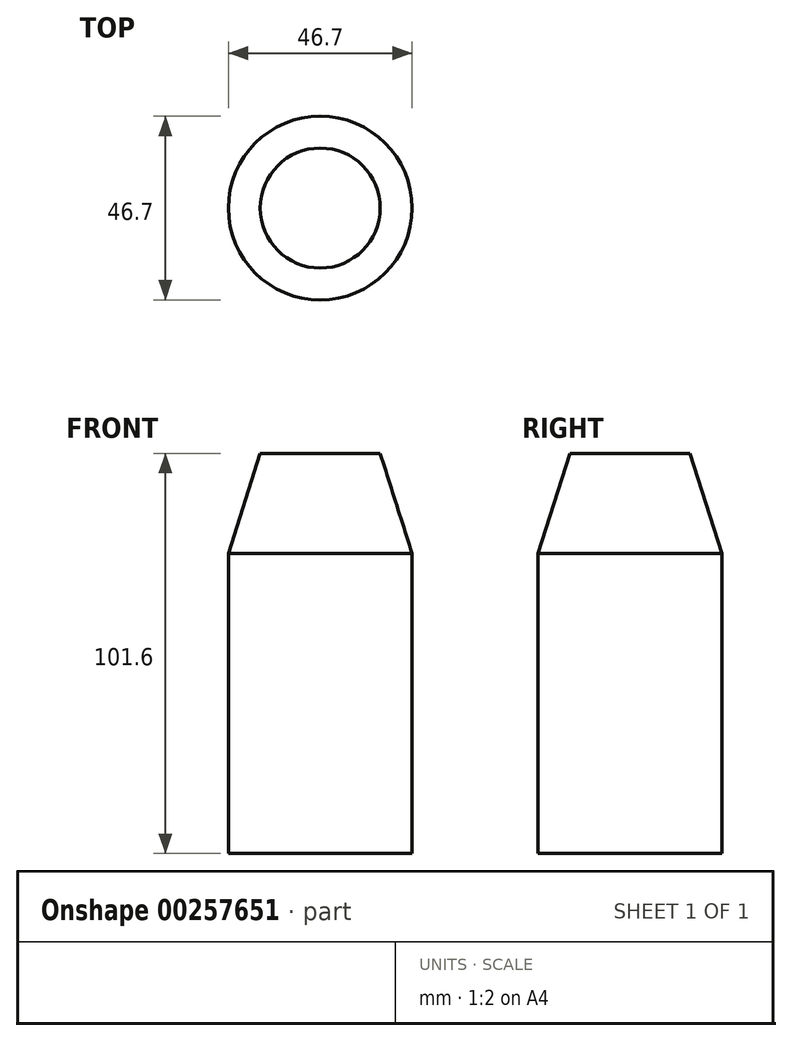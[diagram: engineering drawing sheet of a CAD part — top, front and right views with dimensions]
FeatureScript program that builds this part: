
annotation { "Feature Type Name" : "Feature", "Feature Type Description" : "" }
export const myFeature = defineFeature(function(context is Context, id is Id, definition is map)
    precondition{}
    {
        {
            var Q0;
            Q0=qCreatedBy(makeId("Top.planeOp"),FACE);
            var sketch = newSketch(context, id + "F0", { "sketchPlane" : qUnion([Q0])});
            skCircle(sketch, "E0", {"center": v(0, 0) * mm, "radius": 23.35 * mm});
            skSolve(sketch);
        }
        {
            var Q0;
            Q0=makeQuery(id+"F0.imprint","IMPRINT",FACE,{"disambiguationData":[TD([[makeQuery(id+"F0.imprint","IMPRINT",EDGE,{"derivedFrom":sQuery(id+"F0.wireOp",EDGE,"E0")}),1.0]])]});
            extrude(context, id + "F1", {"entities" : qUnion([Q0]), "depth" : 76.2 * mm});
        }
        {
            var Q0;
            Q0=makeQuery(id+"F1.opExtrude","CAP_FACE",FACE,{"disambiguationData":[OSD([sQuery(id+"F0.wireOp",EDGE,"E0")])],"isStart":false});
            cPlane(context, id + "F2", {"entities" : qUnion([Q0]), "cplaneType" : CPlaneType.OFFSET, "offset" : 25.4 * mm, "width" : 152.4 * mm, "height" : 152.4 * mm});
        }
        {
            var Q0;
            Q0=qCreatedBy(id+"F2.planeOp",FACE);
            var sketch = newSketch(context, id + "F3", { "sketchPlane" : qUnion([Q0])});
            skCircle(sketch, "E1", {"center": v(0, 0) * mm, "radius": 15.24 * mm});
            skSolve(sketch);
        }
        {
            var Q1;
            Q1=makeQuery(id+"F3.imprint","IMPRINT",FACE,{"disambiguationData":[TD([[makeQuery(id+"F3.imprint","IMPRINT",EDGE,{"derivedFrom":sQuery(id+"F3.wireOp",EDGE,"E1")}),1.0]])]});
            var Q2;
            Q2=makeQuery(id+"F1.opExtrude","CAP_FACE",FACE,{"disambiguationData":[OSD([sQuery(id+"F0.wireOp",EDGE,"E0")])],"isStart":false});
            loft(context, id + "F4", {"operationType" : NewBodyOperationType.ADD, "sheetProfilesArray" : [{ "sheetProfileEntities" : qUnion([Q1]) }, { "sheetProfileEntities" : qUnion([Q2]) }]});
        }
    });
